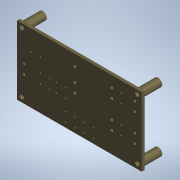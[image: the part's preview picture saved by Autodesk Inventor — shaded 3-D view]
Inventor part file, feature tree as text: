
AUTODESK INVENTOR PART (.ipt)
format: ipt  version: 2022.1 (Build 261234000, 234)  size: 190,976 bytes
history: native  units: mm (DEFAULTED — no unit token found)
features: other x9, sketch x2, hole x1, extrude x1, projected_geometry x1
bodies: Body1 (feature_tree)
feature tree (14):
  other  "Board"
  other  "Sólido1"
  other  "Origen"
  hole  "Agujero1"  [1 undecoded]
  extrude  "Extrusión1"  Depth=1.0mm
  other  "Plano YZ"
  other  "Plano XZ"
  other  "Plano XY"
  other  "Eje X"
  other  "Eje Y"
  other  "Eje Z"
  sketch  "Boceto1"  dims[d0=2.4mm d1=6.0mm d2=4.4mm d3=2.0mm d4=16.0mm d5=8.0mm d6=20.594885mm d7=1.0mm]
  projected_geometry  "Contorno proyectado1"
  sketch  "Boceto2"  dims[d8=1.0mm d9=1.0mm d10=1.0mm d11=10.0mm d12=0.0mm]
note: 1 required parameter value undecoded (feature->parameter linkage not recoverable at this tier; creation-order binding heuristic only, values carry confidence <= 0.55)
